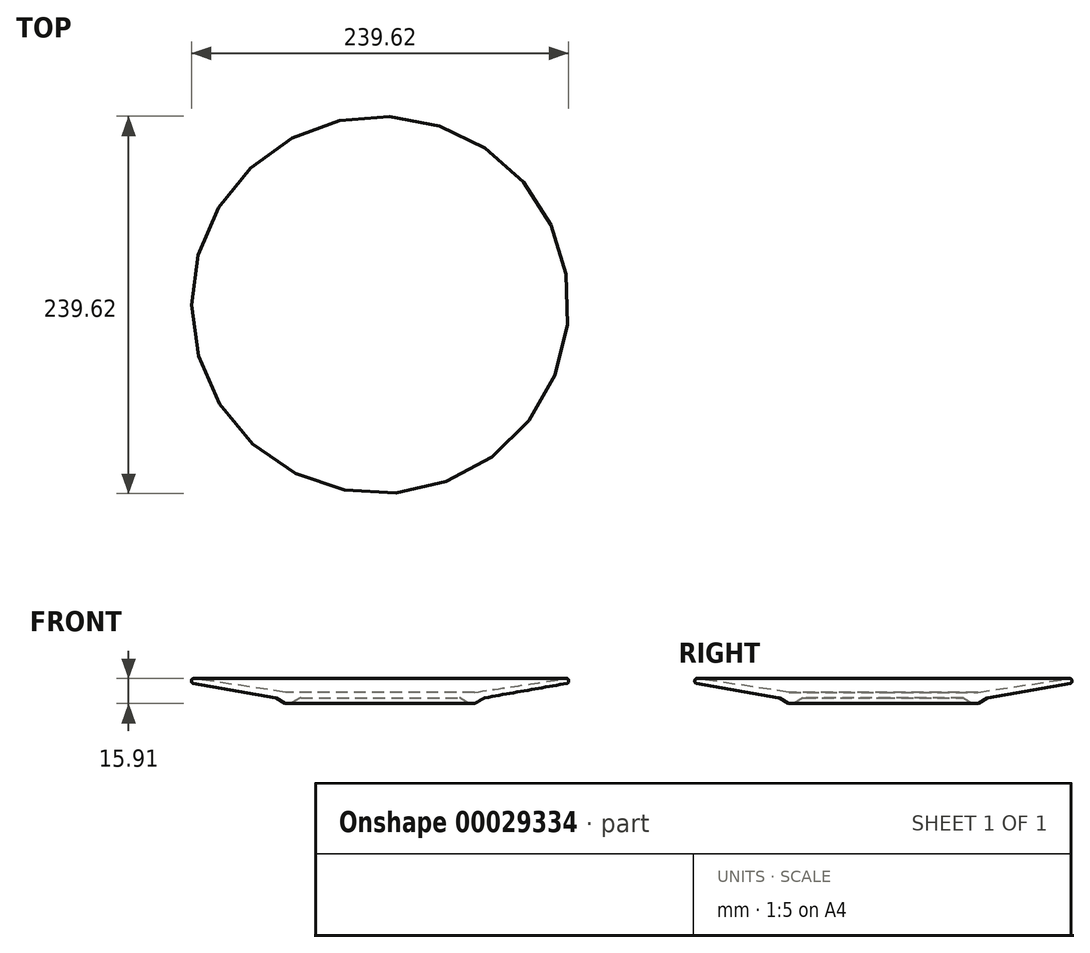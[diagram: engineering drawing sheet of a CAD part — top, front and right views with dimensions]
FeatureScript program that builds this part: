
annotation { "Feature Type Name" : "Feature", "Feature Type Description" : "" }
export const myFeature = defineFeature(function(context is Context, id is Id, definition is map)
    precondition{}
    {
        {
            var Q0;
            Q0=qCreatedBy(makeId("Front.planeOp"),FACE);
            var sketch = newSketch(context, id + "F0", { "sketchPlane" : qUnion([Q0])});
            skLineSegment(sketch, "E0", {"start": v(0, 0) * mm, "end": v(0, 0) * mm});
            skLineSegment(sketch, "E1", {"start": v(-120, 13.11) * mm, "end": v(-119.48, 16.06) * mm});
            skLineSegment(sketch, "E2", {"start": v(0, 7.18) * mm, "end": v(-60, 7.18) * mm});
            skLineSegment(sketch, "E3", {"start": v(-60, 7.18) * mm, "end": v(-119.48, 16.06) * mm});
            skLineSegment(sketch, "E4", {"start": v(-120, 13.11) * mm, "end": v(-66.31, 3.64) * mm});
            skLineSegment(sketch, "E5", {"start": v(-66.31, 3.64) * mm, "end": v(-60, 0) * mm});
            skLineSegment(sketch, "E6", {"start": v(-60, 0) * mm, "end": v(-57, 0) * mm});
            skLineSegment(sketch, "E7", {"start": v(-57, 0) * mm, "end": v(-50.69, 3.64) * mm});
            skLineSegment(sketch, "E8", {"start": v(-50.69, 3.64) * mm, "end": v(0, 3.64) * mm});
            skLineSegment(sketch, "E9", {"start": v(0, 7.18) * mm, "end": v(0, 3.64) * mm});
            skLineSegment(sketch, "E10", {"start": v(0, 3.64) * mm, "end": v(0, 0) * mm, "construction": true});
            skLineSegment(sketch, "E11", {"start": v(-57, 0) * mm, "end": v(0, 0) * mm, "construction": true});
            skLineSegment(sketch, "E12", {"start": v(-66.31, 3.64) * mm, "end": v(-50.69, 3.64) * mm, "construction": true});
            skSolve(sketch);
        }
        {
            var Q0;
            Q0=makeQuery(id+"F0.imprint","IMPRINT",FACE,{"disambiguationData":[TD([[makeQuery(id+"F0.imprint","IMPRINT",EDGE,{"derivedFrom":sQuery(id+"F0.wireOp",EDGE,"E1")}),-1.0]])]});
            var Q1;
            Q1=sQuery(id+"F0.wireOp",EDGE,"E9");
            revolve(context, id + "F1", {"entities" : qUnion([Q0]), "axis" : qUnion([Q1]), "revolveType" : RevolveType.FULL});
        }
        {
            var Q0;
            Q0=makeQuery(id+"F1.opRevolve","SWEPT_EDGE",EDGE,{"disambiguationData":[OSD([sQuery(id+"F0.wireOp",EDGE,"E1"),sQuery(id+"F0.wireOp",EDGE,"E3")])]});
            var Q1;
            Q1=makeQuery(id+"F1.opRevolve","SWEPT_EDGE",EDGE,{"disambiguationData":[OSD([sQuery(id+"F0.wireOp",EDGE,"E1"),sQuery(id+"F0.wireOp",EDGE,"E4")])]});
            var Q2;
            Q2=makeQuery(id+"F1.opRevolve","SWEPT_EDGE",EDGE,{"disambiguationData":[OSD([sQuery(id+"F0.wireOp",EDGE,"E4"),sQuery(id+"F0.wireOp",EDGE,"E5")])]});
            var Q3;
            Q3=makeQuery(id+"F1.opRevolve","SWEPT_EDGE",EDGE,{"disambiguationData":[OSD([sQuery(id+"F0.wireOp",EDGE,"E7"),sQuery(id+"F0.wireOp",EDGE,"E8")])]});
            var Q4;
            Q4=makeQuery(id+"F1.opRevolve","SWEPT_EDGE",EDGE,{"disambiguationData":[OSD([sQuery(id+"F0.wireOp",EDGE,"E6"),sQuery(id+"F0.wireOp",EDGE,"E7")])]});
            var Q5;
            Q5=makeQuery(id+"F1.opRevolve","SWEPT_EDGE",EDGE,{"disambiguationData":[OSD([sQuery(id+"F0.wireOp",EDGE,"E5"),sQuery(id+"F0.wireOp",EDGE,"E6")])]});
            var Q6;
            Q6=makeQuery(id+"F1.opRevolve","SWEPT_EDGE",EDGE,{"disambiguationData":[OSD([sQuery(id+"F0.wireOp",EDGE,"E2"),sQuery(id+"F0.wireOp",EDGE,"E3")])]});
            fillet(context, id + "F2", {"entities" : qUnion([Q0, Q1, Q2, Q3, Q4, Q5, Q6]), "radius" : 1.2 * mm, "tangentPropagation" : true, "allowEdgeOverflow" : false});
        }
    });
